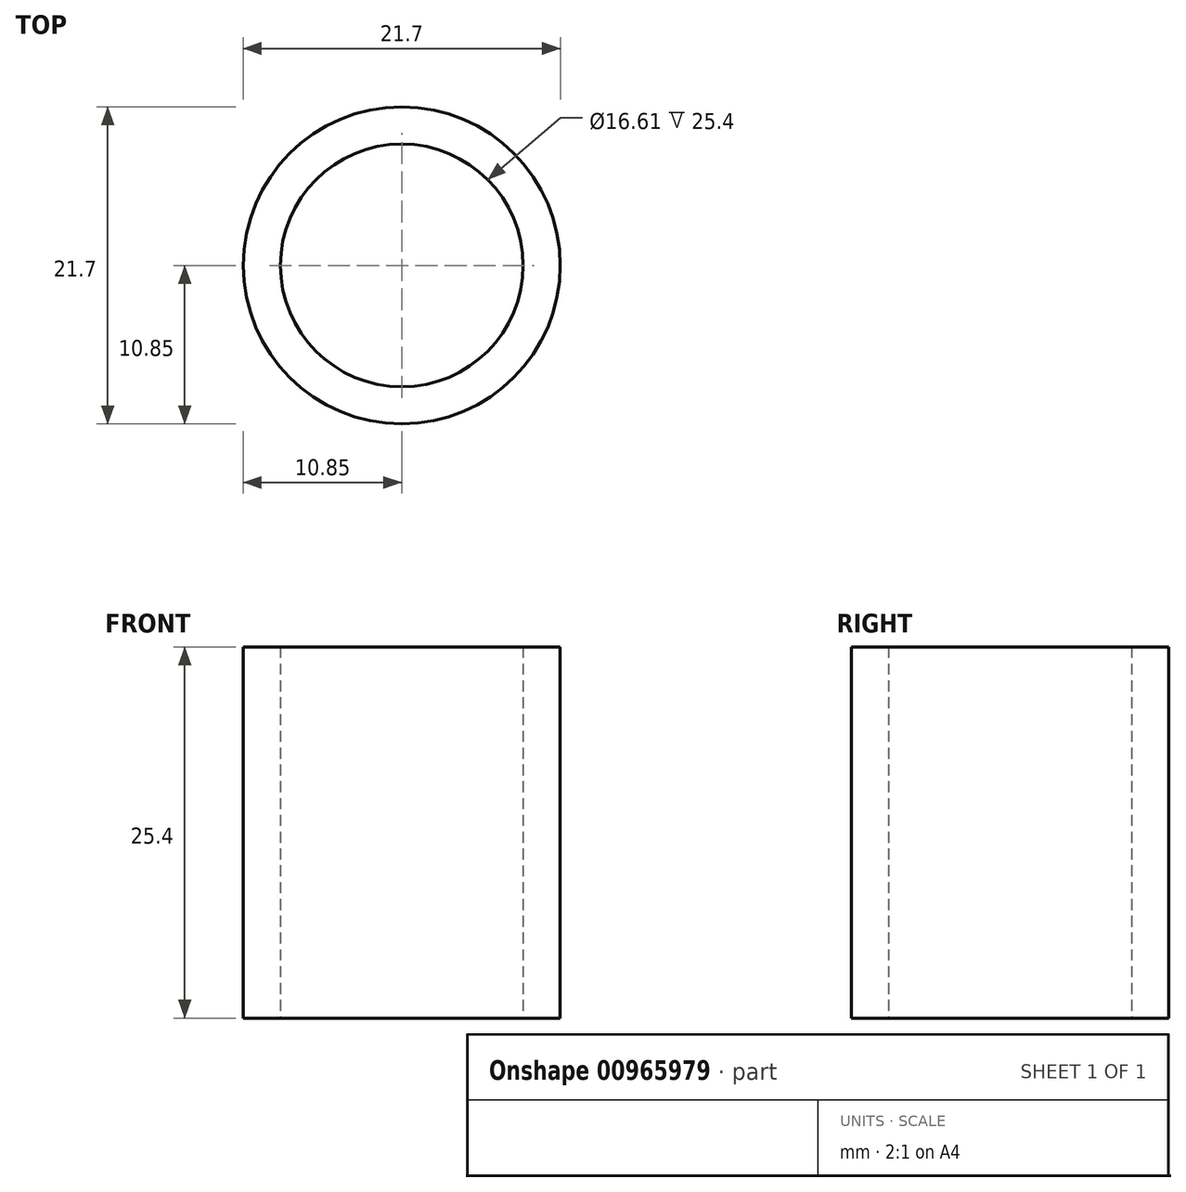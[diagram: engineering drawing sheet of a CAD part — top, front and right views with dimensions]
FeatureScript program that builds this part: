
annotation { "Feature Type Name" : "Feature", "Feature Type Description" : "" }
export const myFeature = defineFeature(function(context is Context, id is Id, definition is map)
    precondition{}
    {
        {
            var Q0;
            Q0=qCreatedBy(makeId("Top.planeOp"),FACE);
            var sketch = newSketch(context, id + "F0", { "sketchPlane" : qUnion([Q0])});
            skCircle(sketch, "E0", {"center": v(0, 0) * mm, "radius": 8.3 * mm});
            skCircle(sketch, "E1", {"center": v(0, 0) * mm, "radius": 10.85 * mm});
            skSolve(sketch);
        }
        {
            var Q0;
            Q0=makeQuery(id+"F0.imprint","IMPRINT",FACE,{"disambiguationData":[TD([[makeQuery(id+"F0.imprint","IMPRINT",EDGE,{"derivedFrom":sQuery(id+"F0.wireOp",EDGE,"E0")}),-1.0]])]});
            extrude(context, id + "F1", {"entities" : qUnion([Q0]), "depth" : 25.4 * mm, "offsetDistance" : 25.4 * mm});
        }
    });
